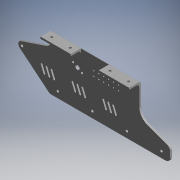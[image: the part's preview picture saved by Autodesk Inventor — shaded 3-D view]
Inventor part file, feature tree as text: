
AUTODESK INVENTOR PART (.ipt)
format: ipt  version: 2019 (Build 230136000, 136)  size: 275,968 bytes
history: native  units: mm (DEFAULTED — no unit token found)
features: extrude x3, fillet x3, sketch x3
ambient origin geometry x8: Origin, YZ Plane, XZ Plane, XY Plane, X Axis, Y Axis, Z Axis, Center Point
bodies: Body1 (feature_tree)
feature tree (9):
  extrude  "Extrusion4"  Depth=22.0mm
  extrude  "Extrusion5"  Depth=50.0mm
  extrude  "Extrusion6"  Depth=4.5mm
  fillet  "Fillet1"  Radius=40.0mm
  fillet  "Fillet2"  Radius=44.7mm
  fillet  "Fillet3"  Radius=190.0mm
  sketch  "Sketch1"  dims[d0=195.0mm d1=22.0mm]
  sketch  "Sketch2"  dims[d2=89.0mm d3=50.0mm]
  sketch  "Sketch3"  dims[d5=143.5mm d6=22.5mm d7=40.0mm d11=44.7mm d12=190.0mm d13=6.0mm d14=7.0mm d15=20.0mm d16=10.0mm d19=4.0mm d20=4.0mm d21=4.0mm d22=4.0mm d23=168.0mm d24=56.0mm d25=56.0mm d26=56.0mm d27=10.0mm d28=14.0mm d29=4.0mm d32=7.0mm d33=59.2mm d34=100.0mm d35=3.5mm d36=3.5mm d37=16.5mm d40=3.0mm d41=3.0mm d42=12.0mm d43=30.0mm d45=8.0mm d46=10.0mm d48=10.0mm d50=30.0mm d52=50.0mm d53=10.0mm d55=10.0mm d57=2.0mm d58=20.0mm d60=8.0mm d61=60.0mm d63=8.0mm d66=3.0mm d67=0.0mm d68=49.0mm d69=3.0mm d70=49.0mm d71=3.0mm d72=16.5mm d73=0.0mm d74=4.0mm d75=4.0mm d76=16.5mm d77=8.25mm d78=4.0mm d79=4.0mm d80=30.0mm d81=30.0mm d82=16.5mm d83=0.0mm d84=4.5mm d85=4.5mm d86=4.5mm d87=25.0mm]
